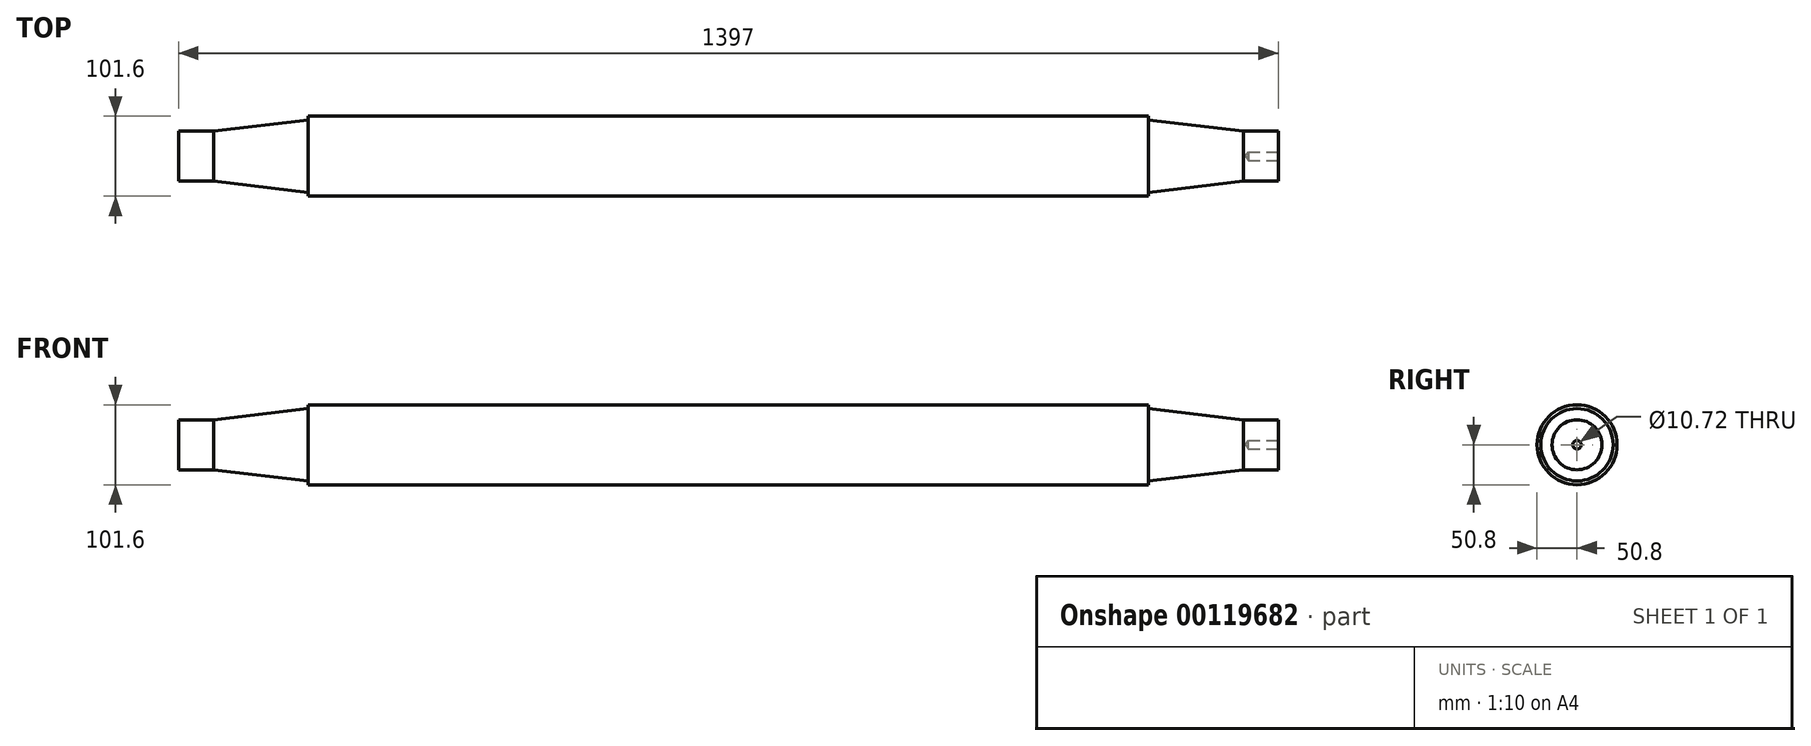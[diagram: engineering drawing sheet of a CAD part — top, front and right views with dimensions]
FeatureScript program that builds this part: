
annotation { "Feature Type Name" : "Feature", "Feature Type Description" : "" }
export const myFeature = defineFeature(function(context is Context, id is Id, definition is map)
    precondition{}
    {
        {
            var Q0;
            Q0=qCreatedBy(makeId("Front.planeOp"),FACE);
            var sketch = newSketch(context, id + "F0", { "sketchPlane" : qUnion([Q0])});
            skLineSegment(sketch, "E0", {"start": v(-698.5, 0) * mm, "end": v(698.5, 0) * mm});
            skLineSegment(sketch, "E1.0", {"start": v(-533.97, 50.8) * mm, "end": v(533.4, 50.8) * mm});
            skLineSegment(sketch, "E2.0", {"start": v(-698.5, 31.75) * mm, "end": v(-654.05, 31.75) * mm});
            skLineSegment(sketch, "E3", {"start": v(-698.5, 31.75) * mm, "end": v(-698.5, 0) * mm});
            skLineSegment(sketch, "E4", {"start": v(-533.4, 45.97) * mm, "end": v(-654.05, 31.75) * mm});
            skLineSegment(sketch, "E5", {"start": v(-533.4, 45.97) * mm, "end": v(-533.97, 50.8) * mm});
            skLineSegment(sketch, "E6", {"start": v(0, 0) * mm, "end": v(0, -221) * mm, "construction": true});
            skLineSegment(sketch, "E7.MirrorCS", {"start": v(698.5, 31.75) * mm, "end": v(698.5, 0) * mm});
            skLineSegment(sketch, "E8.MirrorCS", {"start": v(698.5, 31.75) * mm, "end": v(654.05, 31.75) * mm});
            skLineSegment(sketch, "E9.MirrorCS", {"start": v(533.4, 45.97) * mm, "end": v(654.05, 31.75) * mm});
            skLineSegment(sketch, "E10", {"start": v(533.4, 45.97) * mm, "end": v(533.4, 50.8) * mm});
            skSolve(sketch);
        }
        {
            var Q0;
            Q0=qSketchRegion(id+"F0",true);
            var Q1;
            Q1=sQuery(id+"F0.wireOp",EDGE,"E0");
            revolve(context, id + "F1", {"entities" : qUnion([Q0]), "axis" : qUnion([Q1]), "revolveType" : RevolveType.FULL});
        }
        {
            var Q0;
            Q0=makeQuery(id+"F1.opRevolve","SWEPT_FACE",FACE,{"disambiguationData":[OSD([sQuery(id+"F0.wireOp",EDGE,"E7.MirrorCS")])]});
            var sketch = newSketch(context, id + "F2", { "sketchPlane" : qUnion([Q0])});
            skCircle(sketch, "E11.0", {"center": v(0, 0) * mm, "radius": 31.75 * mm, "construction": true});
            skSolve(sketch);
        }
        {
            var Q0;
            Q0=sQuery(id+"F2.wireOp",VERTEX,"E11.0.center");
            var Q1;
            Q1=makeQuery(id+"F1.opRevolve","SWEPT_BODY",BODY,{"disambiguationData":[OSD([sQuery(id+"F0.wireOp",EDGE,"E0"),sQuery(id+"F0.wireOp",EDGE,"E1.0"),sQuery(id+"F0.wireOp",EDGE,"E2.0"),sQuery(id+"F0.wireOp",EDGE,"E3"),sQuery(id+"F0.wireOp",EDGE,"E4"),sQuery(id+"F0.wireOp",EDGE,"E5"),sQuery(id+"F0.wireOp",EDGE,"E7.MirrorCS"),sQuery(id+"F0.wireOp",EDGE,"E8.MirrorCS"),sQuery(id+"F0.wireOp",EDGE,"E9.MirrorCS"),sQuery(id+"F0.wireOp",EDGE,"E10")])]});
            hole(context, id + "F3", {"style" : HoleStyle.SIMPLE, "endStyle" : HoleEndStyle.BLIND, "standardTappedOrClearance" : lookupTablePath({ "standard" : "ANSI", "engagement" : "75%", "pitch" : "13 tpi", "size" : "1/2", "type" : "Tapped" }), "standardBlindInLast" : lookupTablePath({ "standard" : "ANSI", "engagement" : "75%", "pitch" : "13 tpi", "size" : "1/2", "type" : "Tapped" }), "holeDiameter" : 10.72 * mm, "holeDepth" : 38.1 * mm, "locations" : qUnion([Q0]), "scope" : qUnion([Q1]), "majorDiameter" : 12.7 * mm});
        }
    });
